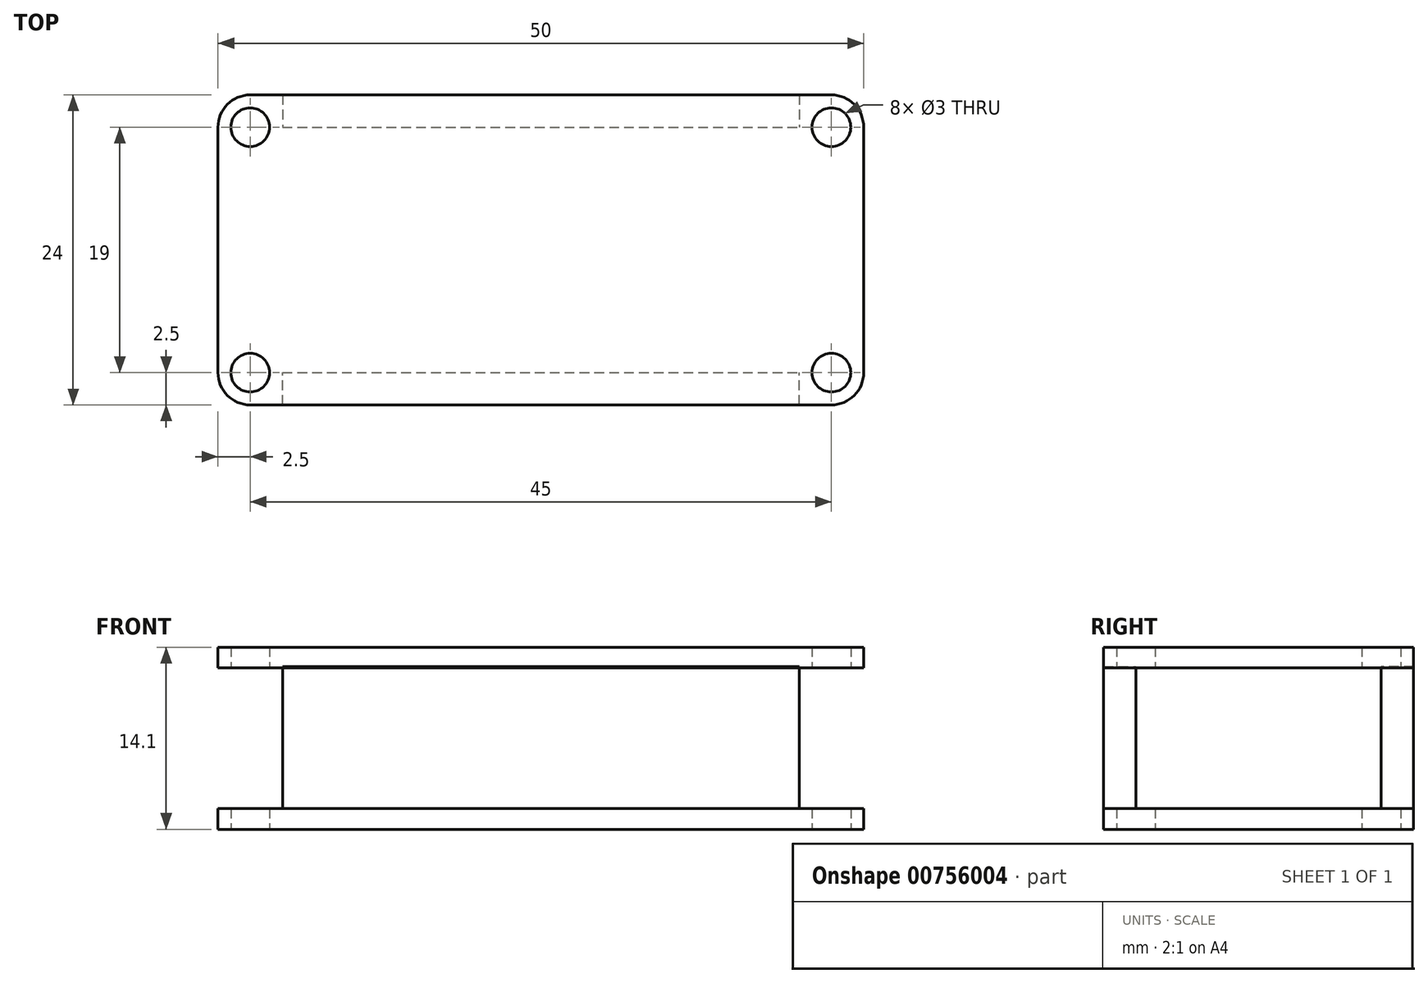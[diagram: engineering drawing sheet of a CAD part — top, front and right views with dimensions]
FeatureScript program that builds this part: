
annotation { "Feature Type Name" : "Feature", "Feature Type Description" : "" }
export const myFeature = defineFeature(function(context is Context, id is Id, definition is map)
    precondition{}
    {
        {
            var Q0;
            Q0=qCreatedBy(makeId("Top.planeOp"),FACE);
            var sketch = newSketch(context, id + "F0", { "sketchPlane" : qUnion([Q0])});
            skLineSegment(sketch, "E0.bottom", {"start": v(22.5, -12) * mm, "end": v(-22.5, -12) * mm});
            skLineSegment(sketch, "E0.top", {"start": v(22.5, 12) * mm, "end": v(-22.5, 12) * mm});
            skLineSegment(sketch, "E0.left", {"start": v(25, -9.5) * mm, "end": v(25, 9.5) * mm});
            skLineSegment(sketch, "E0.right", {"start": v(-25, -9.5) * mm, "end": v(-25, 9.5) * mm});
            skPoint(sketch, "E0.middle", {"position": v(0, 0) * mm});
            skPoint(sketch, "E1.visualSharp", {"position": v(-25, 12) * mm});
            skArc(sketch, "E1.filletArc", {"start": v(-22.5, 12) * mm, "mid": v(-24.27, 11.27) * mm, "end": v(-25, 9.5) * mm});
            skPoint(sketch, "E2.visualSharp", {"position": v(-25, -12) * mm});
            skArc(sketch, "E2.filletArc", {"start": v(-25, -9.5) * mm, "mid": v(-24.27, -11.27) * mm, "end": v(-22.5, -12) * mm});
            skPoint(sketch, "E3.visualSharp", {"position": v(25, -12) * mm});
            skArc(sketch, "E3.filletArc", {"start": v(22.5, -12) * mm, "mid": v(24.27, -11.27) * mm, "end": v(25, -9.5) * mm});
            skPoint(sketch, "E4.visualSharp", {"position": v(25, 12) * mm});
            skArc(sketch, "E4.filletArc", {"start": v(25, 9.5) * mm, "mid": v(24.27, 11.27) * mm, "end": v(22.5, 12) * mm});
            skCircle(sketch, "E5", {"center": v(-22.5, 9.5) * mm, "radius": 1.5 * mm});
            skLineSegment(sketch, "E6", {"start": v(0, 0) * mm, "end": v(0, -12) * mm, "construction": true});
            skLineSegment(sketch, "E7", {"start": v(0, 0) * mm, "end": v(-25, 0) * mm, "construction": true});
            skCircle(sketch, "E8.MirrorC", {"center": v(-22.5, -9.5) * mm, "radius": 1.5 * mm});
            skCircle(sketch, "E9.MirrorC", {"center": v(22.5, -9.5) * mm, "radius": 1.5 * mm});
            skCircle(sketch, "E10.MirrorC", {"center": v(22.5, 9.5) * mm, "radius": 1.5 * mm});
            skSolve(sketch);
        }
        {
            var Q0;
            Q0=makeQuery(id+"F0.imprint","IMPRINT",FACE,{"disambiguationData":[TD([[makeQuery(id+"F0.imprint","IMPRINT",EDGE,{"derivedFrom":sQuery(id+"F0.wireOp",EDGE,"E0.bottom")}),-1.0]])]});
            extrude(context, id + "F1", {"entities" : qUnion([Q0]), "depth" : 1.6 * mm, "offsetDistance" : 25 * mm});
        }
        {
            var Q0;
            Q0=makeQuery(id+"F1.opExtrude","CAP_FACE",FACE,{"disambiguationData":[OSD([sQuery(id+"F0.wireOp",EDGE,"E0.bottom"),sQuery(id+"F0.wireOp",EDGE,"E0.top"),sQuery(id+"F0.wireOp",EDGE,"E0.left"),sQuery(id+"F0.wireOp",EDGE,"E0.right"),sQuery(id+"F0.wireOp",EDGE,"E1.filletArc"),sQuery(id+"F0.wireOp",EDGE,"E2.filletArc"),sQuery(id+"F0.wireOp",EDGE,"E3.filletArc"),sQuery(id+"F0.wireOp",EDGE,"E4.filletArc"),sQuery(id+"F0.wireOp",EDGE,"E5"),sQuery(id+"F0.wireOp",EDGE,"E8.MirrorC"),sQuery(id+"F0.wireOp",EDGE,"E9.MirrorC"),sQuery(id+"F0.wireOp",EDGE,"E10.MirrorC")])],"isStart":false});
            var sketch = newSketch(context, id + "F2", { "sketchPlane" : qUnion([Q0])});
            skLineSegment(sketch, "E11.bottom", {"start": v(-20, -12) * mm, "end": v(20, -12) * mm});
            skLineSegment(sketch, "E11.top", {"start": v(-20, -9.5) * mm, "end": v(20, -9.5) * mm});
            skLineSegment(sketch, "E11.left", {"start": v(-20, -12) * mm, "end": v(-20, -9.5) * mm});
            skLineSegment(sketch, "E11.right", {"start": v(20, -12) * mm, "end": v(20, -9.5) * mm});
            skLineSegment(sketch, "E12", {"start": v(0, 0) * mm, "end": v(25, 0) * mm, "construction": true});
            skLineSegment(sketch, "E13.MirrorCS", {"start": v(-20, 9.5) * mm, "end": v(20, 9.5) * mm});
            skLineSegment(sketch, "E14.MirrorCS", {"start": v(-20, 12) * mm, "end": v(-20, 9.5) * mm});
            skLineSegment(sketch, "E15.MirrorCS", {"start": v(-20, 12) * mm, "end": v(20, 12) * mm});
            skLineSegment(sketch, "E16.MirrorCS", {"start": v(20, 12) * mm, "end": v(20, 9.5) * mm});
            skSolve(sketch);
        }
        {
            var Q0;
            Q0 = qSketchRegion(id + "F2", true);
            extrude(context, id + "F3", {"entities" : qUnion([Q0]), "depth" : 11 * mm, "offsetDistance" : 25 * mm});
        }
        {
            var Q0;
            Q0=makeQuery(id+"F1.opExtrude","SWEPT_BODY",BODY,{"disambiguationData":[OSD([sQuery(id+"F0.wireOp",EDGE,"E0.bottom"),sQuery(id+"F0.wireOp",EDGE,"E0.top"),sQuery(id+"F0.wireOp",EDGE,"E0.left"),sQuery(id+"F0.wireOp",EDGE,"E0.right"),sQuery(id+"F0.wireOp",EDGE,"E1.filletArc"),sQuery(id+"F0.wireOp",EDGE,"E2.filletArc"),sQuery(id+"F0.wireOp",EDGE,"E3.filletArc"),sQuery(id+"F0.wireOp",EDGE,"E4.filletArc"),sQuery(id+"F0.wireOp",EDGE,"E5"),sQuery(id+"F0.wireOp",EDGE,"E8.MirrorC"),sQuery(id+"F0.wireOp",EDGE,"E9.MirrorC"),sQuery(id+"F0.wireOp",EDGE,"E10.MirrorC")])]});
            transform(context, id + "F4", {"entities" : qUnion([Q0]), "transformType" : TransformType.TRANSLATION_3D, "dx" : 0 * mm, "dy" : 0 * mm, "dz" : 12.5 * mm, "makeCopy" : true});
        }
    });
